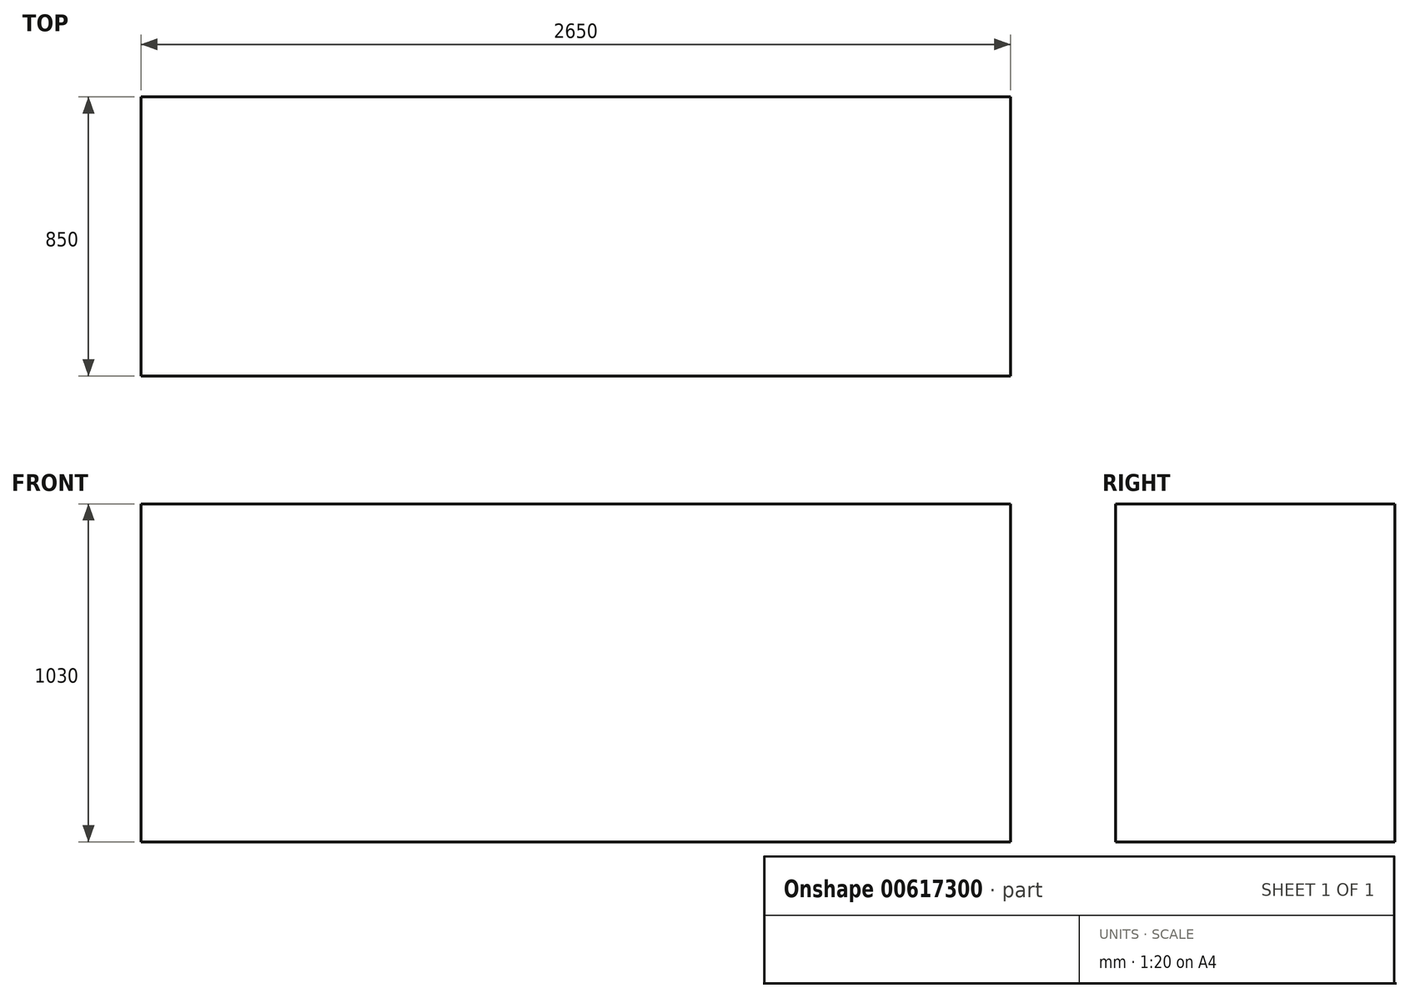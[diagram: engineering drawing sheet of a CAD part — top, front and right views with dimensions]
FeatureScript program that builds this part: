
annotation { "Feature Type Name" : "Feature", "Feature Type Description" : "" }
export const myFeature = defineFeature(function(context is Context, id is Id, definition is map)
    precondition{}
    {
        {
            var Q0;
            Q0=qCreatedBy(makeId("Top.planeOp"),FACE);
            var sketch = newSketch(context, id + "F0", { "sketchPlane" : qUnion([Q0])});
            skLineSegment(sketch, "E0.bottom", {"start": v(-2265.67, -478.2) * mm, "end": v(384.33, -478.2) * mm});
            skLineSegment(sketch, "E0.top", {"start": v(-2265.67, -1328.2) * mm, "end": v(384.33, -1328.2) * mm});
            skLineSegment(sketch, "E0.left", {"start": v(-2265.67, -478.2) * mm, "end": v(-2265.67, -1328.2) * mm});
            skLineSegment(sketch, "E0.right", {"start": v(384.33, -478.2) * mm, "end": v(384.33, -1328.2) * mm});
            skSolve(sketch);
        }
        {
            var Q0;
            Q0 = qSketchRegion(id + "F0", true);
            extrude(context, id + "F1", {"entities" : qUnion([Q0]), "depth" : 1030 * mm, "offsetDistance" : 25 * mm});
        }
    });
